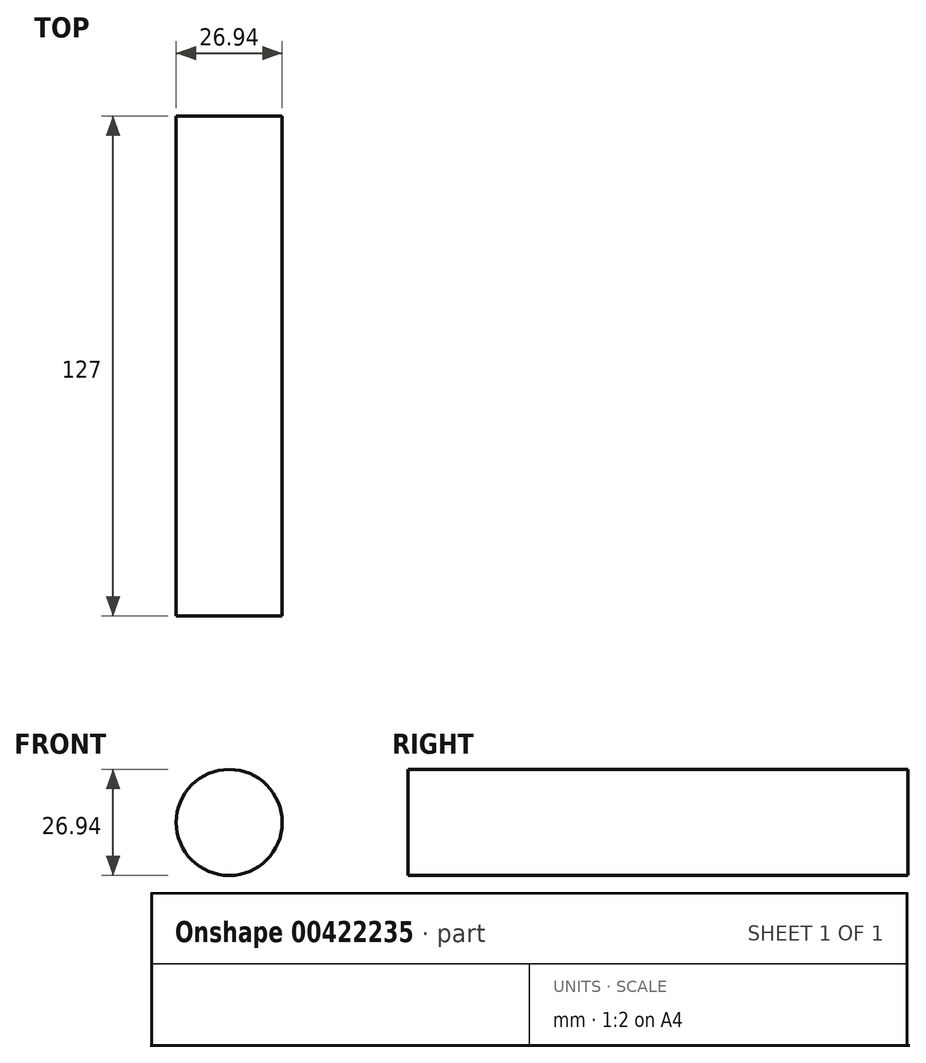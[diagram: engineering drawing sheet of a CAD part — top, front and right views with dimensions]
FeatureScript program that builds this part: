
annotation { "Feature Type Name" : "Feature", "Feature Type Description" : "" }
export const myFeature = defineFeature(function(context is Context, id is Id, definition is map)
    precondition{}
    {
        {
            var Q0;
            Q0=qCreatedBy(makeId("Front.planeOp"),FACE);
            var sketch = newSketch(context, id + "F0", { "sketchPlane" : qUnion([Q0])});
            skCircle(sketch, "E0", {"center": v(0, 0) * mm, "radius": 13.47 * mm});
            skSolve(sketch);
        }
        {
            var Q0;
            Q0=makeQuery(id+"F0.imprint","IMPRINT",FACE,{"disambiguationData":[TD([[makeQuery(id+"F0.imprint","IMPRINT",EDGE,{"derivedFrom":sQuery(id+"F0.wireOp",EDGE,"E0")}),1.0]])]});
            extrude(context, id + "F1", {"entities" : qUnion([Q0]), "depth" : 127 * mm});
        }
    });
